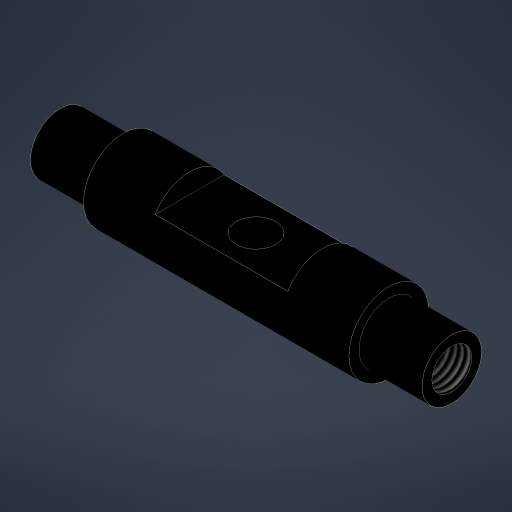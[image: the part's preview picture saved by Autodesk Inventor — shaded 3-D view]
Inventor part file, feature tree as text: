
AUTODESK INVENTOR PART (.ipt)
format: ipt  version: 2025 (Build 290162010, 162A)  size: 218,112 bytes
history: native  units: mm
features: extrude x7, sketch x4, thread x2
ambient origin geometry x8: Origin, YZ Plane, XZ Plane, XY Plane, X Axis, Y Axis, Z Axis, Center Point
bodies: Solid1 (feature_tree)
feature tree (13):
  extrude  "Extrusion1"  Depth=29.5mm TaperAngle=0.0deg
  extrude  "Extrusion2"  Depth=3.0mm
  extrude  "Extrusion3"  Depth=4.5mm
  extrude  "Extrusion4"  Depth=3.0mm
  extrude  "Extrusion5"  Depth=3.0mm TaperAngle=0.0deg
  thread  "Thread1"  [1 undecoded]
  thread  "Thread2"  [1 undecoded]
  extrude  "Extrusion6"  Depth=10.0mm TaperAngle=0.0deg
  extrude  "Extrusion7"  Depth=3.0mm
  sketch  "Sketch2"  dims[d0=6.0mm d1=29.5mm d2=0.0mm]
  sketch  "Sketch4"  dims[d3=4.5mm d4=3.0mm]
  sketch  "Sketch6"  dims[d5=4.75mm d6=0.0mm d7=4.5mm]
  sketch  "Sketch7"  dims[d8=3.0mm d9=6.0mm d10=4.75mm d11=0.0mm d12=1.5mm d13=7.0mm d14=10.0mm d15=0.0mm d16=3.0mm d17=0.0mm d18=0.0mm d19=4.75mm d20=0.0mm d21=4.75mm d22=0.0mm d23=2.0mm d24=0.0mm d25=2.0mm d26=0.0mm]
note: 2 required parameter values undecoded (feature->parameter linkage not recoverable at this tier; creation-order binding heuristic only, values carry confidence <= 0.55)
